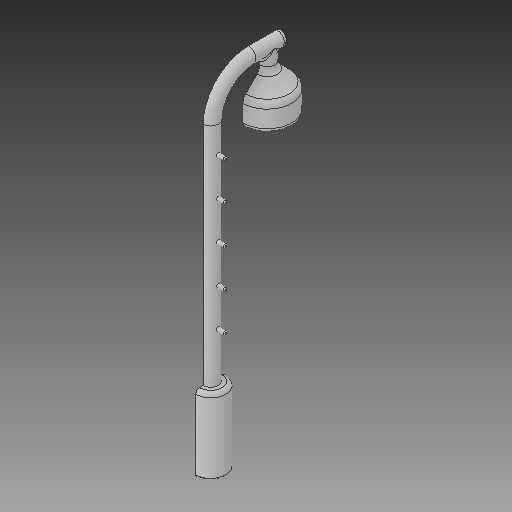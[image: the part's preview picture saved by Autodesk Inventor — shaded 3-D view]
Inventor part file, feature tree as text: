
AUTODESK INVENTOR PART (.ipt)
format: ipt  version: 2018 (Build 220112000, 112)  size: 303,616 bytes
history: native  units: in
note: dims shown in document units (in); Inventor stores cm internally (conversion verified against a paired STEP export)
features: other x3, sketch x2
ambient origin geometry x8: Origin, YZ Plane, XZ Plane, XY Plane, X Axis, Y Axis, Z Axis, Center Point
bodies: Solid1 (feature_tree)
feature tree (5):
  other  "lampa_nadrazni.ipt"
  other  "Solid1::lampa_nadrazni.ipt"
  other  "TaggingFeature1"
  sketch  "Sketch1"  dims[d0=0.3937in]
  sketch  "Sketch11"
